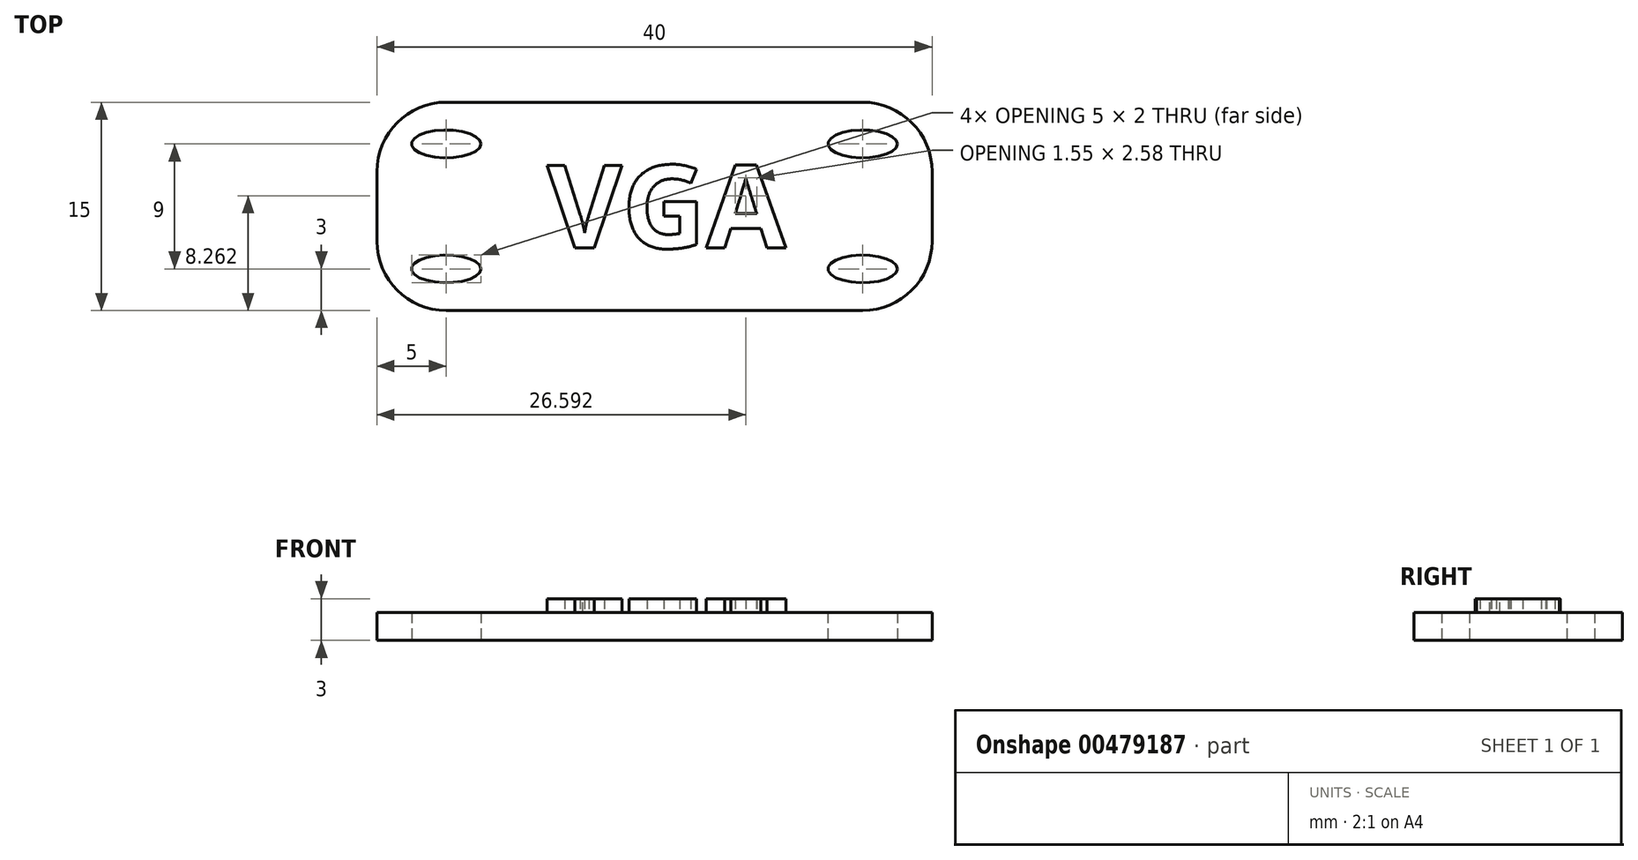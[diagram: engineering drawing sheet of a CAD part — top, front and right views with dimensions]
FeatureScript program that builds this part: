
annotation { "Feature Type Name" : "Feature", "Feature Type Description" : "" }
export const myFeature = defineFeature(function(context is Context, id is Id, definition is map)
    precondition{}
    {
        {
            var Q0;
            Q0=qCreatedBy(makeId("Top.planeOp"),FACE);
            var sketch = newSketch(context, id + "F0", { "sketchPlane" : qUnion([Q0])});
            skLineSegment(sketch, "E0.bottom", {"start": v(20, -7.5) * mm, "end": v(-20, -7.5) * mm});
            skLineSegment(sketch, "E0.top", {"start": v(20, 7.5) * mm, "end": v(-20, 7.5) * mm});
            skLineSegment(sketch, "E0.left", {"start": v(20, -7.5) * mm, "end": v(20, 7.5) * mm});
            skLineSegment(sketch, "E0.right", {"start": v(-20, -7.5) * mm, "end": v(-20, 7.5) * mm});
            skPoint(sketch, "E0.middle", {"position": v(0, 0) * mm});
            skLineSegment(sketch, "E1", {"start": v(-20, -4.5) * mm, "end": v(20, -4.5) * mm, "construction": true});
            skPoint(sketch, "E2", {"position": v(-15, -4.5) * mm});
            skEllipse(sketch, "E3", {"center": v(-15, -4.5) * mm, "majorRadius": 2.5 * mm, "minorRadius": 1 * mm, "majorAxis": v(1, 0)});
            skEllipse(sketch, "E4.1.0.0", {"center": v(15, -4.5) * mm, "majorRadius": 2.5 * mm, "minorRadius": 1 * mm, "majorAxis": v(1, 0)});
            skLineSegment(sketch, "E4.direction1", {"start": v(-15, -4.5) * mm, "end": v(15, -4.5) * mm, "construction": true});
            skLineSegment(sketch, "E5", {"start": v(20, 0) * mm, "end": v(-20, 0) * mm, "construction": true});
            skEllipse(sketch, "E6.MirrorC", {"center": v(15, 4.5) * mm, "majorRadius": 2.5 * mm, "minorRadius": 1 * mm, "majorAxis": v(1, 0)});
            skEllipse(sketch, "E7.MirrorC", {"center": v(-15, 4.5) * mm, "majorRadius": 2.5 * mm, "minorRadius": 1 * mm, "majorAxis": v(1, 0)});
            skSolve(sketch);
        }
        {
            var Q0;
            Q0=makeQuery(id+"F0.imprint","IMPRINT",FACE,{"disambiguationData":[TD([[makeQuery(id+"F0.imprint","IMPRINT",EDGE,{"derivedFrom":sQuery(id+"F0.wireOp",EDGE,"E0.bottom")}),-1.0]])]});
            extrude(context, id + "F1", {"entities" : qUnion([Q0]), "depth" : 2 * mm});
        }
        {
            var Q0;
            Q0=makeQuery(id+"F1.opExtrude","CAP_FACE",FACE,{"disambiguationData":[OSD([sQuery(id+"F0.wireOp",EDGE,"E0.bottom"),sQuery(id+"F0.wireOp",EDGE,"E0.top"),sQuery(id+"F0.wireOp",EDGE,"E0.left"),sQuery(id+"F0.wireOp",EDGE,"E0.right"),sQuery(id+"F0.wireOp",EDGE,"E3"),sQuery(id+"F0.wireOp",EDGE,"E4.1.0.0"),sQuery(id+"F0.wireOp",EDGE,"E6.MirrorC"),sQuery(id+"F0.wireOp",EDGE,"E7.MirrorC")])],"isStart":false});
            var sketch = newSketch(context, id + "F2", { "sketchPlane" : qUnion([Q0])});
            skText(sketch, "E8", { "text": "VGA", "fontName": "OpenSans-Bold.ttf"});
            const initialGuessF2  = {"E8": [-0.00774, -0.003, 1, 0, 0.006]};
            skSetInitialGuess(sketch, initialGuessF2);
            skSolve(sketch);
        }
        {
            var Q0;
            Q0 = qSketchRegion(id + "F2", true);
            extrude(context, id + "F3", {"entities" : qUnion([Q0]), "depth" : 1 * mm});
        }
        {
            var Q0;
            Q0=makeQuery(id+"F1.opExtrude","SWEPT_EDGE",EDGE,{"disambiguationData":[OSD([sQuery(id+"F0.wireOp",EDGE,"E0.top"),sQuery(id+"F0.wireOp",EDGE,"E0.right")])]});
            var Q1;
            Q1=makeQuery(id+"F1.opExtrude","SWEPT_EDGE",EDGE,{"disambiguationData":[OSD([sQuery(id+"F0.wireOp",EDGE,"E0.top"),sQuery(id+"F0.wireOp",EDGE,"E0.left")])]});
            var Q2;
            Q2=makeQuery(id+"F1.opExtrude","SWEPT_EDGE",EDGE,{"disambiguationData":[OSD([sQuery(id+"F0.wireOp",EDGE,"E0.bottom"),sQuery(id+"F0.wireOp",EDGE,"E0.right")])]});
            var Q3;
            Q3=makeQuery(id+"F1.opExtrude","SWEPT_EDGE",EDGE,{"disambiguationData":[OSD([sQuery(id+"F0.wireOp",EDGE,"E0.bottom"),sQuery(id+"F0.wireOp",EDGE,"E0.left")])]});
            fillet(context, id + "F4", {"entities" : qUnion([Q0, Q1, Q2, Q3]), "radius" : 5 * mm, "tangentPropagation" : true, "allowEdgeOverflow" : false});
        }
    });
